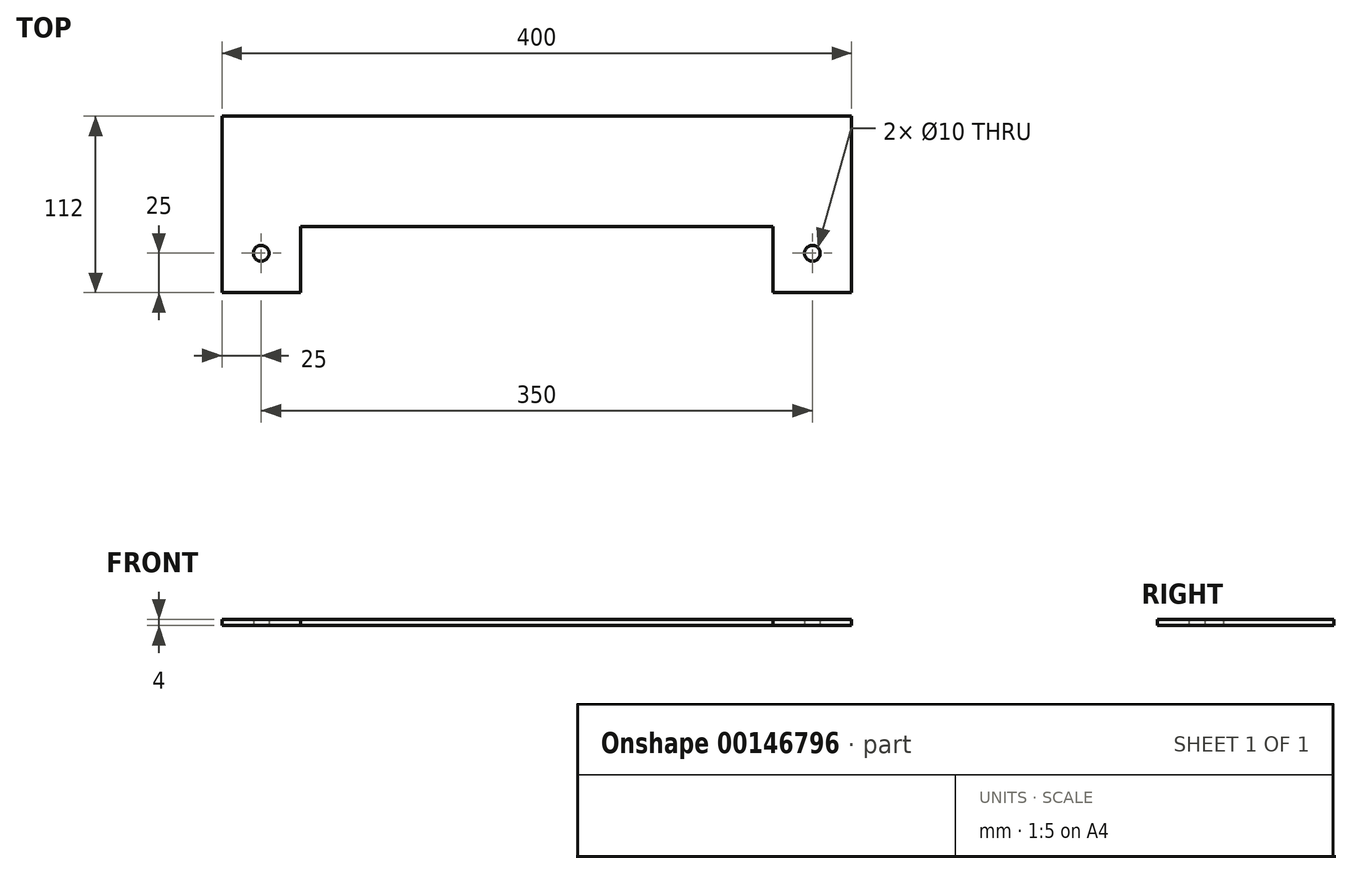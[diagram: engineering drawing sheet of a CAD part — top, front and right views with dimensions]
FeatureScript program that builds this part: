
annotation { "Feature Type Name" : "Feature", "Feature Type Description" : "" }
export const myFeature = defineFeature(function(context is Context, id is Id, definition is map)
    precondition{}
    {
        {
            var Q0;
            Q0=qCreatedBy(makeId("Top.planeOp"),FACE);
            var sketch = newSketch(context, id + "F0", { "sketchPlane" : qUnion([Q0])});
            skLineSegment(sketch, "E0.bottom", {"start": v(0, 0) * mm, "end": v(400, 0) * mm});
            skLineSegment(sketch, "E0.top", {"start": v(50, -70) * mm, "end": v(350, -70) * mm});
            skLineSegment(sketch, "E0.left", {"start": v(0, 0) * mm, "end": v(0, -112) * mm});
            skLineSegment(sketch, "E0.right", {"start": v(400, 0) * mm, "end": v(400, -112) * mm});
            skPoint(sketch, "E0.middle", {"position": v(0, 0) * mm});
            skLineSegment(sketch, "E1", {"start": v(50, -70) * mm, "end": v(50, -112) * mm});
            skLineSegment(sketch, "E2", {"start": v(350, -70) * mm, "end": v(350, -112) * mm});
            skLineSegment(sketch, "E3", {"start": v(50, -112) * mm, "end": v(0, -112) * mm});
            skLineSegment(sketch, "E4", {"start": v(400, -112) * mm, "end": v(350, -112) * mm});
            skCircle(sketch, "E5", {"center": v(25, -87) * mm, "radius": 5 * mm});
            skCircle(sketch, "E6", {"center": v(375, -87) * mm, "radius": 5 * mm});
            skSolve(sketch);
        }
        {
            var Q0;
            Q0=makeQuery(id+"F0.imprint","IMPRINT",FACE,{"disambiguationData":[TD([[makeQuery(id+"F0.imprint","IMPRINT",EDGE,{"derivedFrom":sQuery(id+"F0.wireOp",EDGE,"E0.bottom")}),-1.0]])]});
            extrude(context, id + "F1", {"entities" : qUnion([Q0]), "depth" : 4 * mm});
        }
    });
